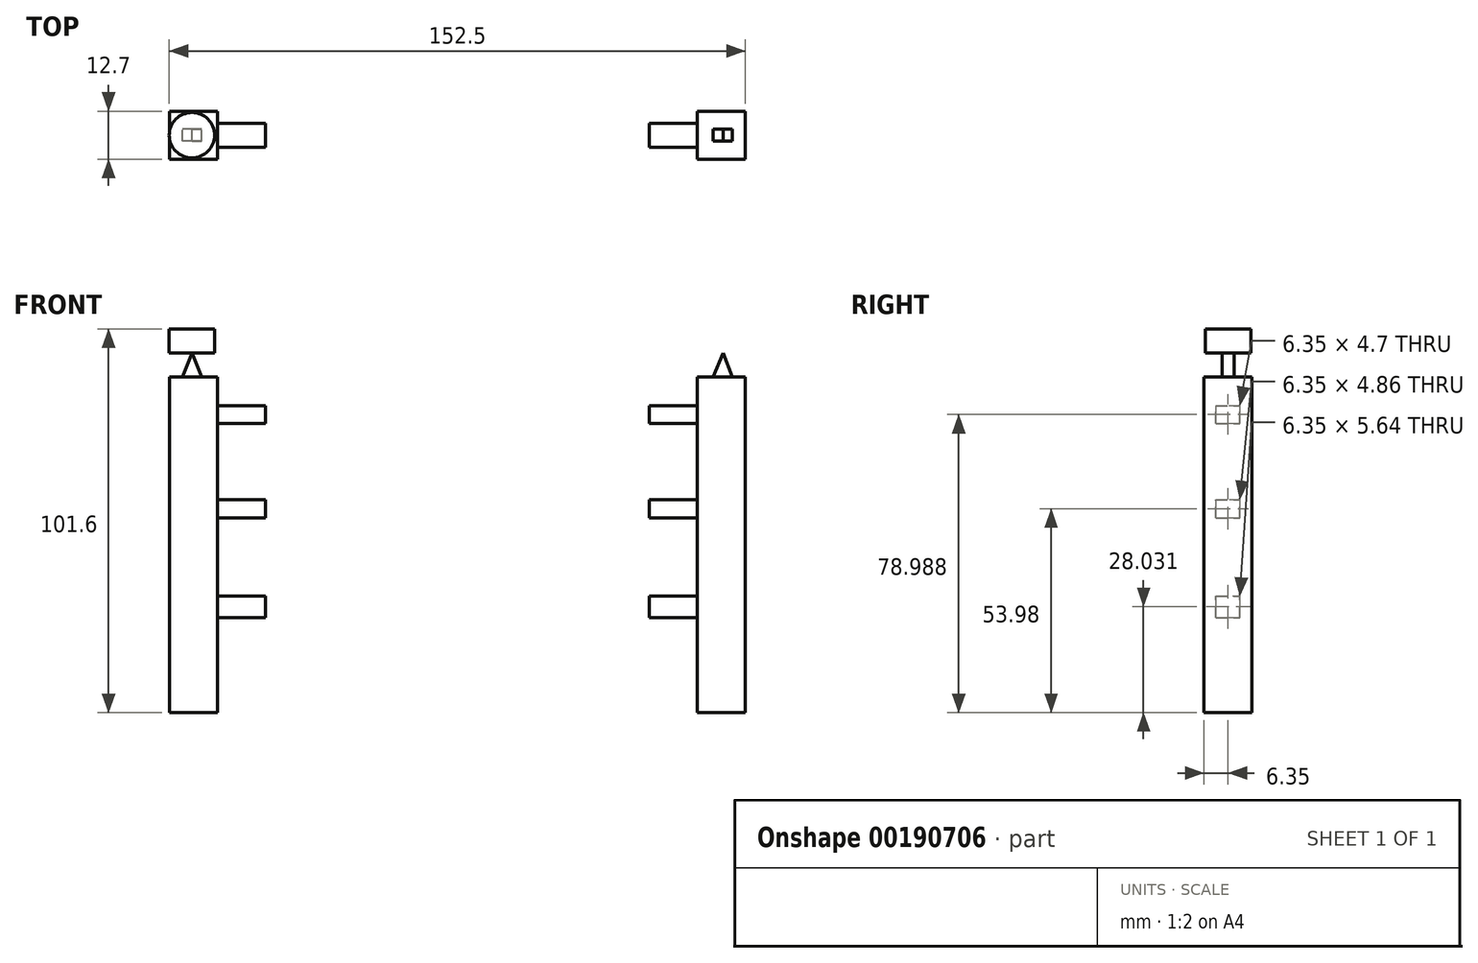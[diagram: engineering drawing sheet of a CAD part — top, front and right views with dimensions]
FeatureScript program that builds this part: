
annotation { "Feature Type Name" : "Feature", "Feature Type Description" : "" }
export const myFeature = defineFeature(function(context is Context, id is Id, definition is map)
    precondition{}
    {
        {
            var Q0;
            Q0=qCreatedBy(makeId("Front.planeOp"),FACE);
            var sketch = newSketch(context, id + "F0", { "sketchPlane" : qUnion([Q0])});
            skLineSegment(sketch, "E0.bottom", {"start": v(-63.5, -56.41) * mm, "end": v(-76.2, -56.41) * mm});
            skLineSegment(sketch, "E0.top", {"start": v(-63.5, 32.49) * mm, "end": v(-76.2, 32.49) * mm});
            skLineSegment(sketch, "E0.left", {"start": v(-63.5, -56.41) * mm, "end": v(-63.5, 32.49) * mm});
            skLineSegment(sketch, "E0.right", {"start": v(-76.2, -56.41) * mm, "end": v(-76.2, 32.49) * mm});
            skLineSegment(sketch, "E1.bottom", {"start": v(-76.3, 45.19) * mm, "end": v(-64.27, 45.19) * mm});
            skLineSegment(sketch, "E1.top", {"start": v(-76.3, 38.84) * mm, "end": v(-64.27, 38.84) * mm});
            skLineSegment(sketch, "E1.left", {"start": v(-76.3, 45.19) * mm, "end": v(-76.3, 38.84) * mm});
            skLineSegment(sketch, "E1.right", {"start": v(-64.27, 45.19) * mm, "end": v(-64.27, 38.84) * mm});
            skLineSegment(sketch, "E2.bottom", {"start": v(-63.5, 24.93) * mm, "end": v(-50.8, 24.93) * mm});
            skLineSegment(sketch, "E2.top", {"start": v(-63.5, 20.23) * mm, "end": v(-50.8, 20.23) * mm});
            skLineSegment(sketch, "E2.left", {"start": v(-63.5, 24.93) * mm, "end": v(-63.5, 20.23) * mm});
            skLineSegment(sketch, "E2.right", {"start": v(-50.8, 24.93) * mm, "end": v(-50.8, 20.23) * mm});
            skLineSegment(sketch, "E3.bottom", {"start": v(-63.5, 0) * mm, "end": v(-50.8, 0) * mm});
            skLineSegment(sketch, "E3.top", {"start": v(-63.5, -4.86) * mm, "end": v(-50.8, -4.86) * mm});
            skLineSegment(sketch, "E3.left", {"start": v(-63.5, 0) * mm, "end": v(-63.5, -4.86) * mm});
            skLineSegment(sketch, "E3.right", {"start": v(-50.8, 0) * mm, "end": v(-50.8, -4.86) * mm});
            skLineSegment(sketch, "E4.bottom", {"start": v(-63.5, -25.56) * mm, "end": v(-50.8, -25.56) * mm});
            skLineSegment(sketch, "E4.top", {"start": v(-63.5, -31.2) * mm, "end": v(-50.8, -31.2) * mm});
            skLineSegment(sketch, "E4.left", {"start": v(-63.5, -25.56) * mm, "end": v(-63.5, -31.2) * mm});
            skLineSegment(sketch, "E4.right", {"start": v(-50.8, -25.56) * mm, "end": v(-50.8, -31.2) * mm});
            skLineSegment(sketch, "E5", {"start": v(-70.28, 45.19) * mm, "end": v(-70.28, 38.84) * mm});
            skLineSegment(sketch, "E6", {"start": v(-70.28, 38.84) * mm, "end": v(-72.74, 32.49) * mm});
            skLineSegment(sketch, "E7", {"start": v(-70.28, 38.84) * mm, "end": v(-67.68, 32.49) * mm});
            skSolve(sketch);
        }
        {
            var Q0;
            {var subQ4=sQuery(id+"F0.wireOp",EDGE,"E0.bottom");Q0=makeQuery(id+"F0.imprint","IMPRINT",FACE,{"disambiguationData":[TD([[makeQuery(id+"F0.imprint","IMPRINT",EDGE,{"derivedFrom":subQ4}),-1.0]])]});}
            extrude(context, id + "F1", {"entities" : qUnion([Q0]), "endBound" : BoundingType.SYMMETRIC, "depth" : 12.7 * mm});
        }
        {
            var Q0;
            Q0=makeQuery(id+"F0.imprint","IMPRINT",FACE,{"disambiguationData":[TD([[makeQuery(id+"F0.imprint","IMPRINT",EDGE,{"derivedFrom":sQuery(id+"F0.wireOp",EDGE,"E2.bottom")}),-1.0]])]});
            var Q1;
            Q1=makeQuery(id+"F0.imprint","IMPRINT",FACE,{"disambiguationData":[TD([[makeQuery(id+"F0.imprint","IMPRINT",EDGE,{"derivedFrom":sQuery(id+"F0.wireOp",EDGE,"E3.bottom")}),-1.0]])]});
            var Q2;
            Q2=makeQuery(id+"F0.imprint","IMPRINT",FACE,{"disambiguationData":[TD([[makeQuery(id+"F0.imprint","IMPRINT",EDGE,{"derivedFrom":sQuery(id+"F0.wireOp",EDGE,"E4.bottom")}),-1.0]])]});
            extrude(context, id + "F2", {"entities" : qUnion([Q0, Q1, Q2]), "operationType" : NewBodyOperationType.ADD, "endBound" : BoundingType.SYMMETRIC, "depth" : 6.35 * mm});
        }
        {
            var Q0;
            {var subQ0=sQuery(id+"F0.wireOp",EDGE,"E1.right");Q0=makeQuery(id+"F0.imprint","IMPRINT",FACE,{"disambiguationData":[TD([[makeQuery(id+"F0.imprint","IMPRINT",EDGE,{"derivedFrom":subQ0}),-1.0]])]});}
            var Q1;
            Q1=sQuery(id+"F0.wireOp",EDGE,"E5");
            revolve(context, id + "F3", {"entities" : qUnion([Q0]), "axis" : qUnion([Q1]), "revolveType" : RevolveType.FULL});
        }
        {
            var Q0;
            {var subQ0=sQuery(id+"F0.wireOp",EDGE,"E6");Q0=makeQuery(id+"F0.imprint","IMPRINT",FACE,{"disambiguationData":[TD([[makeQuery(id+"F0.imprint","IMPRINT",EDGE,{"derivedFrom":subQ0}),1.0]])]});}
            extrude(context, id + "F4", {"entities" : qUnion([Q0]), "operationType" : NewBodyOperationType.ADD, "endBound" : BoundingType.SYMMETRIC, "depth" : 3.17 * mm});
        }
        {
            var Q0;
            Q0=makeQuery(id+"F1.opExtrude","SWEPT_BODY",BODY,{"disambiguationData":[OSD([sQuery(id+"F0.wireOp",EDGE,"E0.bottom"),sQuery(id+"F0.wireOp",EDGE,"E0.top"),sQuery(id+"F0.wireOp",EDGE,"E0.left"),sQuery(id+"F0.wireOp",EDGE,"E0.right"),sQuery(id+"F0.wireOp",EDGE,"E2.left"),sQuery(id+"F0.wireOp",EDGE,"E3.left"),sQuery(id+"F0.wireOp",EDGE,"E4.left")])]});
            var Q1;
            Q1=qCreatedBy(makeId("Right.planeOp"),FACE);
            mirror(context, id + "F5", {"entities" : qUnion([Q0]), "mirrorPlane" : qUnion([Q1])});
        }
    });
